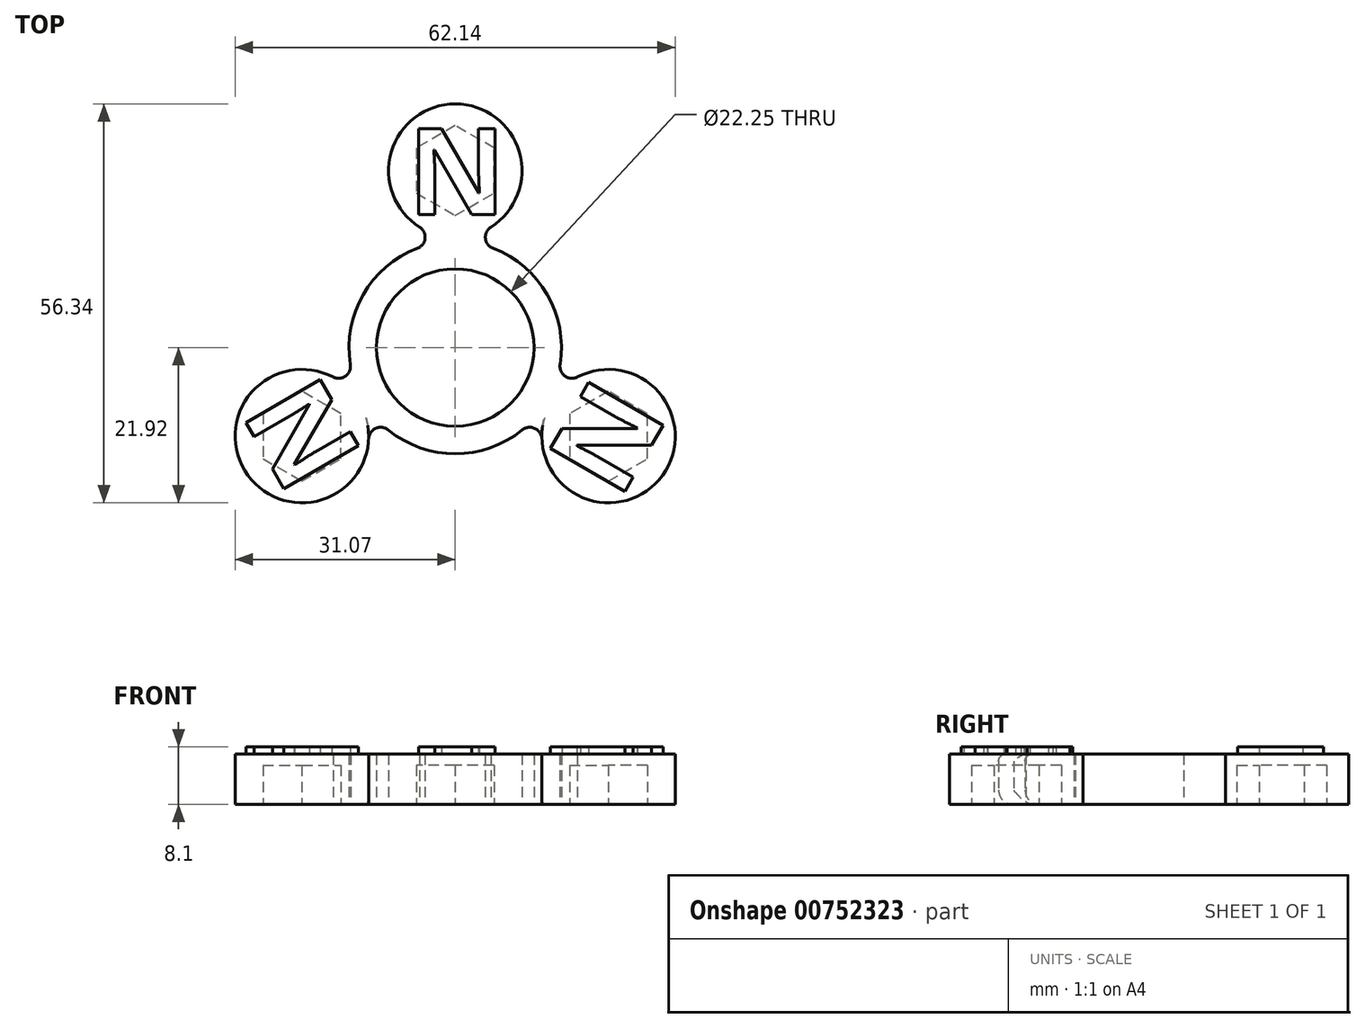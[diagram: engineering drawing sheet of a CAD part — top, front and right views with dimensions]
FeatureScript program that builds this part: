
annotation { "Feature Type Name" : "Feature", "Feature Type Description" : "" }
export const myFeature = defineFeature(function(context is Context, id is Id, definition is map)
    precondition{}
    {
        {
            var Q0;
            Q0=qCreatedBy(makeId("Top.planeOp"),FACE);
            var sketch = newSketch(context, id + "F0", { "sketchPlane" : qUnion([Q0])});
            skCircle(sketch, "E0", {"center": v(0, 0) * mm, "radius": 15 * mm});
            skCircle(sketch, "E1", {"center": v(0, 0) * mm, "radius": 11.12 * mm});
            skSolve(sketch);
        }
        {
            var Q0;
            Q0 = qSketchRegion(id + "F0", true);
            extrude(context, id + "F1", {"entities" : qUnion([Q0]), "depth" : 7.1 * mm, "offsetDistance" : 25 * mm});
        }
        {
            var Q0;
            Q0=qCreatedBy(makeId("Top.planeOp"),FACE);
            var sketch = newSketch(context, id + "F2", { "sketchPlane" : qUnion([Q0])});
            skCircle(sketch, "E2", {"center": v(0, 25) * mm, "radius": 9.42 * mm});
            skCircle(sketch, "E3.1.0", {"center": v(-21.65, -12.5) * mm, "radius": 9.42 * mm});
            skCircle(sketch, "E3.2.0", {"center": v(21.65, -12.5) * mm, "radius": 9.42 * mm});
            skPoint(sketch, "E3.center", {"position": v(0, 0) * mm});
            skSolve(sketch);
        }
        {
            var Q0;
            Q0 = qSketchRegion(id + "F2", true);
            extrude(context, id + "F3", {"entities" : qUnion([Q0]), "operationType" : NewBodyOperationType.ADD, "depth" : 7.1 * mm, "offsetDistance" : 25 * mm});
        }
        {
            var Q0;
            Q0=qCreatedBy(makeId("Top.planeOp"),FACE);
            var sketch = newSketch(context, id + "F4", { "sketchPlane" : qUnion([Q0])});
            skArc(sketch, "E4", {"start": v(-5.05, 17.04) * mm, "mid": v(0, 15.58) * mm, "end": v(5.05, 17.04) * mm});
            skArc(sketch, "E5", {"start": v(-5.35, 14.01) * mm, "mid": v(-4.27, 15.43) * mm, "end": v(-5.05, 17.04) * mm});
            skArc(sketch, "E6.MirrorCS", {"start": v(5.35, 14.01) * mm, "mid": v(4.27, 15.43) * mm, "end": v(5.05, 17.04) * mm});
            skArc(sketch, "E7", {"start": v(5.35, 14.01) * mm, "mid": v(0, 15) * mm, "end": v(-5.35, 14.01) * mm});
            skArc(sketch, "E8.1.0", {"start": v(-14.81, -2.37) * mm, "mid": v(-15.5, -4.02) * mm, "end": v(-17.28, -4.15) * mm});
            skArc(sketch, "E8.1.1", {"start": v(-9.46, -11.64) * mm, "mid": v(-11.23, -11.41) * mm, "end": v(-12.23, -12.9) * mm});
            skArc(sketch, "E8.1.2", {"start": v(-14.81, -2.37) * mm, "mid": v(-13, -7.5) * mm, "end": v(-9.46, -11.64) * mm});
            skArc(sketch, "E8.1.3", {"start": v(-12.23, -12.9) * mm, "mid": v(-13.49, -7.79) * mm, "end": v(-17.28, -4.15) * mm});
            skArc(sketch, "E8.2.0", {"start": v(9.46, -11.64) * mm, "mid": v(11.23, -11.41) * mm, "end": v(12.23, -12.9) * mm});
            skArc(sketch, "E8.2.1", {"start": v(14.81, -2.37) * mm, "mid": v(15.5, -4.02) * mm, "end": v(17.28, -4.15) * mm});
            skArc(sketch, "E8.2.2", {"start": v(9.46, -11.64) * mm, "mid": v(13, -7.5) * mm, "end": v(14.81, -2.37) * mm});
            skArc(sketch, "E8.2.3", {"start": v(17.28, -4.15) * mm, "mid": v(13.49, -7.79) * mm, "end": v(12.23, -12.9) * mm});
            skSolve(sketch);
        }
        {
            var Q0;
            Q0 = qSketchRegion(id + "F4", true);
            extrude(context, id + "F5", {"entities" : qUnion([Q0]), "operationType" : NewBodyOperationType.ADD, "depth" : 7.1 * mm, "offsetDistance" : 25 * mm});
        }
        {
            var Q0;
            Q0=makeQuery(id+"F5.boolean.opBoolean","MERGE",FACE,{"derivedFrom":[makeQuery(id+"F1.opExtrude","CAP_FACE",FACE,{"disambiguationData":[OSD([sQuery(id+"F0.wireOp",EDGE,"E0"),sQuery(id+"F0.wireOp",EDGE,"E1")])],"isStart":false}),makeQuery(id+"F3.opExtrude","CAP_FACE",FACE,{"disambiguationData":[OSD([sQuery(id+"F2.wireOp",EDGE,"E2")])],"isStart":false}),makeQuery(id+"F3.opExtrude","CAP_FACE",FACE,{"disambiguationData":[OSD([sQuery(id+"F2.wireOp",EDGE,"E3.1.0")])],"isStart":false}),makeQuery(id+"F3.opExtrude","CAP_FACE",FACE,{"disambiguationData":[OSD([sQuery(id+"F2.wireOp",EDGE,"E3.2.0")])],"isStart":false}),makeQuery(id+"F5.opExtrude","CAP_FACE",FACE,{"disambiguationData":[OSD([sQuery(id+"F4.wireOp",EDGE,"E4"),sQuery(id+"F4.wireOp",EDGE,"E5"),sQuery(id+"F4.wireOp",EDGE,"E6.MirrorCS"),sQuery(id+"F4.wireOp",EDGE,"E7")])],"isStart":false}),makeQuery(id+"F5.opExtrude","CAP_FACE",FACE,{"disambiguationData":[OSD([sQuery(id+"F4.wireOp",EDGE,"E8.1.0"),sQuery(id+"F4.wireOp",EDGE,"E8.1.1"),sQuery(id+"F4.wireOp",EDGE,"E8.1.2"),sQuery(id+"F4.wireOp",EDGE,"E8.1.3")])],"isStart":false}),makeQuery(id+"F5.opExtrude","CAP_FACE",FACE,{"disambiguationData":[OSD([sQuery(id+"F4.wireOp",EDGE,"E8.2.0"),sQuery(id+"F4.wireOp",EDGE,"E8.2.1"),sQuery(id+"F4.wireOp",EDGE,"E8.2.2"),sQuery(id+"F4.wireOp",EDGE,"E8.2.3")])],"isStart":false})]});
            var sketch = newSketch(context, id + "F6", { "sketchPlane" : qUnion([Q0])});
            skText(sketch, "E9", { "text": "N", "fontName": "OpenSans-Bold.ttf"});
            const initialGuessF6  = {"E9": [-0.0067, 0.01876, 1, 0, 0.01226]};
            skSetInitialGuess(sketch, initialGuessF6);
            skSolve(sketch);
        }
        {
            var Q0;
            Q0 = qSketchRegion(id + "F6", true);
            extrude(context, id + "F7", {"entities" : qUnion([Q0]), "depth" : 1 * mm, "offsetDistance" : 25 * mm});
        }
        {
            var Q0;
            Q0=qCreatedBy(makeId("Front.planeOp"),FACE);
            var sketch = newSketch(context, id + "F8", { "sketchPlane" : qUnion([Q0])});
            skLineSegment(sketch, "E10", {"start": v(0, -8.61) * mm, "end": v(0, 37.6) * mm});
            skSolve(sketch);
        }
        {
            var Q0;
            Q0=makeQuery(id+"F7.opExtrude","SWEPT_BODY",BODY,{"disambiguationData":[OSD([sQuery(id+"F6.wireOp",EDGE,"E9.sketch_text.stroke-0"),sQuery(id+"F6.wireOp",EDGE,"E9.sketch_text.stroke-1"),sQuery(id+"F6.wireOp",EDGE,"E9.sketch_text.stroke-2"),sQuery(id+"F6.wireOp",EDGE,"E9.sketch_text.stroke-3"),sQuery(id+"F6.wireOp",EDGE,"E9.sketch_text.stroke-4"),sQuery(id+"F6.wireOp",EDGE,"E9.sketch_text.stroke-5"),sQuery(id+"F6.wireOp",EDGE,"E9.sketch_text.stroke-6"),sQuery(id+"F6.wireOp",EDGE,"E9.sketch_text.stroke-7"),sQuery(id+"F6.wireOp",EDGE,"E9.sketch_text.stroke-8"),sQuery(id+"F6.wireOp",EDGE,"E9.sketch_text.stroke-9"),sQuery(id+"F6.wireOp",EDGE,"E9.sketch_text.stroke-10"),sQuery(id+"F6.wireOp",EDGE,"E9.sketch_text.stroke-11"),sQuery(id+"F6.wireOp",EDGE,"E9.sketch_text.stroke-12"),sQuery(id+"F6.wireOp",EDGE,"E9.sketch_text.stroke-13")])]});
            var Q1;
            Q1=sQuery(id+"F8.wireOp",EDGE,"E10");
            circularPattern(context, id + "F9", {"entities" : qUnion([Q0]), "axis" : qUnion([Q1]), "angle" : 360 * degree, "instanceCount" : 3, "equalSpace" : true, "computeTransformsWithoutBuiltin" : true});
        }
        {
            var Q0;
            Q0=makeQuery(id+"F5.boolean.opBoolean","MERGE",FACE,{"derivedFrom":[makeQuery(id+"F1.opExtrude","CAP_FACE",FACE,{"disambiguationData":[OSD([sQuery(id+"F0.wireOp",EDGE,"E0"),sQuery(id+"F0.wireOp",EDGE,"E1")])],"isStart":true}),makeQuery(id+"F3.opExtrude","CAP_FACE",FACE,{"disambiguationData":[OSD([sQuery(id+"F2.wireOp",EDGE,"E2")])],"isStart":true}),makeQuery(id+"F3.opExtrude","CAP_FACE",FACE,{"disambiguationData":[OSD([sQuery(id+"F2.wireOp",EDGE,"E3.1.0")])],"isStart":true}),makeQuery(id+"F3.opExtrude","CAP_FACE",FACE,{"disambiguationData":[OSD([sQuery(id+"F2.wireOp",EDGE,"E3.2.0")])],"isStart":true}),makeQuery(id+"F5.opExtrude","CAP_FACE",FACE,{"disambiguationData":[OSD([sQuery(id+"F4.wireOp",EDGE,"E4"),sQuery(id+"F4.wireOp",EDGE,"E5"),sQuery(id+"F4.wireOp",EDGE,"E6.MirrorCS"),sQuery(id+"F4.wireOp",EDGE,"E7")])],"isStart":true}),makeQuery(id+"F5.opExtrude","CAP_FACE",FACE,{"disambiguationData":[OSD([sQuery(id+"F4.wireOp",EDGE,"E8.1.0"),sQuery(id+"F4.wireOp",EDGE,"E8.1.1"),sQuery(id+"F4.wireOp",EDGE,"E8.1.2"),sQuery(id+"F4.wireOp",EDGE,"E8.1.3")])],"isStart":true}),makeQuery(id+"F5.opExtrude","CAP_FACE",FACE,{"disambiguationData":[OSD([sQuery(id+"F4.wireOp",EDGE,"E8.2.0"),sQuery(id+"F4.wireOp",EDGE,"E8.2.1"),sQuery(id+"F4.wireOp",EDGE,"E8.2.2"),sQuery(id+"F4.wireOp",EDGE,"E8.2.3")])],"isStart":true})]});
            var sketch = newSketch(context, id + "F10", { "sketchPlane" : qUnion([Q0])});
            skCircle(sketch, "E11.cCircle", {"center": v(0, -25) * mm, "radius": 5.5 * mm, "construction": true});
            skLineSegment(sketch, "E11.0", {"start": v(-5.5, -28.18) * mm, "end": v(-5.5, -21.82) * mm});
            skLineSegment(sketch, "E11.1", {"start": v(-5.5, -21.82) * mm, "end": v(0, -18.65) * mm});
            skLineSegment(sketch, "E11.2", {"start": v(0, -18.65) * mm, "end": v(5.5, -21.82) * mm});
            skLineSegment(sketch, "E11.3", {"start": v(5.5, -21.82) * mm, "end": v(5.5, -28.18) * mm});
            skLineSegment(sketch, "E11.4", {"start": v(5.5, -28.18) * mm, "end": v(0, -31.35) * mm});
            skLineSegment(sketch, "E11.5", {"start": v(0, -31.35) * mm, "end": v(-5.5, -28.18) * mm});
            skPoint(sketch, "E11.0.midPoint", {"position": v(-5.5, -25) * mm});
            skCircle(sketch, "E12.1.0", {"center": v(21.65, 12.5) * mm, "radius": 5.5 * mm, "construction": true});
            skPoint(sketch, "E12.1.1", {"position": v(24.4, 7.74) * mm});
            skLineSegment(sketch, "E12.1.2", {"start": v(27.15, 9.32) * mm, "end": v(21.65, 6.15) * mm});
            skLineSegment(sketch, "E12.1.3", {"start": v(21.65, 6.15) * mm, "end": v(16.15, 9.32) * mm});
            skLineSegment(sketch, "E12.1.4", {"start": v(16.15, 9.32) * mm, "end": v(16.15, 15.68) * mm});
            skLineSegment(sketch, "E12.1.5", {"start": v(16.15, 15.68) * mm, "end": v(21.65, 18.85) * mm});
            skLineSegment(sketch, "E12.1.6", {"start": v(21.65, 18.85) * mm, "end": v(27.15, 15.68) * mm});
            skLineSegment(sketch, "E12.1.7", {"start": v(27.15, 15.68) * mm, "end": v(27.15, 9.32) * mm});
            skCircle(sketch, "E12.2.0", {"center": v(-21.65, 12.5) * mm, "radius": 5.5 * mm, "construction": true});
            skPoint(sketch, "E12.2.1", {"position": v(-18.9, 17.26) * mm});
            skLineSegment(sketch, "E12.2.2", {"start": v(-21.65, 18.85) * mm, "end": v(-16.15, 15.68) * mm});
            skLineSegment(sketch, "E12.2.3", {"start": v(-16.15, 15.68) * mm, "end": v(-16.15, 9.32) * mm});
            skLineSegment(sketch, "E12.2.4", {"start": v(-16.15, 9.32) * mm, "end": v(-21.65, 6.15) * mm});
            skLineSegment(sketch, "E12.2.5", {"start": v(-21.65, 6.15) * mm, "end": v(-27.15, 9.32) * mm});
            skLineSegment(sketch, "E12.2.6", {"start": v(-27.15, 9.32) * mm, "end": v(-27.15, 15.68) * mm});
            skLineSegment(sketch, "E12.2.7", {"start": v(-27.15, 15.68) * mm, "end": v(-21.65, 18.85) * mm});
            skPoint(sketch, "E12.center", {"position": v(0, 0) * mm});
            skSolve(sketch);
        }
        {
            var Q0;
            Q0 = qSketchRegion(id + "F10", true);
            extrude(context, id + "F11", {"entities" : qUnion([Q0]), "operationType" : NewBodyOperationType.REMOVE, "oppositeDirection" : true, "depth" : 5.5 * mm, "offsetDistance" : 25 * mm});
        }
        {
            var Q0;
            {var subQ0=sQuery(id+"F0.wireOp",EDGE,"E0");var subQ1=sQuery(id+"F4.wireOp",EDGE,"E5");Q0=makeQuery(id+"F5.boolean.opBoolean","SPLIT",EDGE,{"disambiguationData":[TD([makeQuery(id+"F5.opExtrude","SWEPT_FACE",FACE,{"disambiguationData":[OSD([subQ1])]})])],"derivedFrom":makeQuery(id+"F1.opExtrude","CAP_EDGE",EDGE,{"disambiguationData":[OSD([subQ0])],"isStart":false})});}
            var Q1;
            {var subQ0=sQuery(id+"F0.wireOp",EDGE,"E0");var subQ2=sQuery(id+"F4.wireOp",EDGE,"E8.1.1");Q1=makeQuery(id+"F5.boolean.opBoolean","SPLIT",EDGE,{"disambiguationData":[TD([makeQuery(id+"F5.opExtrude","SWEPT_FACE",FACE,{"disambiguationData":[OSD([subQ2])]})])],"derivedFrom":makeQuery(id+"F1.opExtrude","CAP_EDGE",EDGE,{"disambiguationData":[OSD([subQ0])],"isStart":false})});}
            var Q2;
            {var subQ0=sQuery(id+"F0.wireOp",EDGE,"E0");var subQ2=sQuery(id+"F4.wireOp",EDGE,"E6.MirrorCS");Q2=makeQuery(id+"F5.boolean.opBoolean","SPLIT",EDGE,{"disambiguationData":[TD([makeQuery(id+"F5.opExtrude","SWEPT_FACE",FACE,{"disambiguationData":[OSD([subQ2])]})])],"derivedFrom":makeQuery(id+"F1.opExtrude","CAP_EDGE",EDGE,{"disambiguationData":[OSD([subQ0])],"isStart":false})});}
            fillet(context, id + "F12", {"entities" : qUnion([Q0, Q1, Q2]), "radius" : 1 * mm, "tangentPropagation" : true, "allowEdgeOverflow" : false});
        }
        {
            var Q0;
            {var subQ0=sQuery(id+"F0.wireOp",EDGE,"E0");var subQ2=sQuery(id+"F4.wireOp",EDGE,"E8.1.1");Q0=makeQuery(id+"F5.boolean.opBoolean","SPLIT",EDGE,{"disambiguationData":[TD([makeQuery(id+"F5.opExtrude","SWEPT_FACE",FACE,{"disambiguationData":[OSD([subQ2])]})])],"derivedFrom":makeQuery(id+"F1.opExtrude","CAP_EDGE",EDGE,{"disambiguationData":[OSD([subQ0])],"isStart":true})});}
            var Q1;
            {var subQ0=sQuery(id+"F0.wireOp",EDGE,"E0");var subQ2=sQuery(id+"F4.wireOp",EDGE,"E6.MirrorCS");Q1=makeQuery(id+"F5.boolean.opBoolean","SPLIT",EDGE,{"disambiguationData":[TD([makeQuery(id+"F5.opExtrude","SWEPT_FACE",FACE,{"disambiguationData":[OSD([subQ2])]})])],"derivedFrom":makeQuery(id+"F1.opExtrude","CAP_EDGE",EDGE,{"disambiguationData":[OSD([subQ0])],"isStart":true})});}
            var Q2;
            {var subQ1=sQuery(id+"F4.wireOp",EDGE,"E5");var subQ2=sQuery(id+"F0.wireOp",EDGE,"E0");Q2=makeQuery(id+"F5.boolean.opBoolean","SPLIT",EDGE,{"disambiguationData":[TD([makeQuery(id+"F5.opExtrude","SWEPT_FACE",FACE,{"disambiguationData":[OSD([subQ1])]})])],"derivedFrom":makeQuery(id+"F1.opExtrude","CAP_EDGE",EDGE,{"disambiguationData":[OSD([subQ2])],"isStart":true})});}
            fillet(context, id + "F13", {"entities" : qUnion([Q0, Q1, Q2]), "radius" : 2 * mm, "tangentPropagation" : true, "allowEdgeOverflow" : false});
        }
    });
